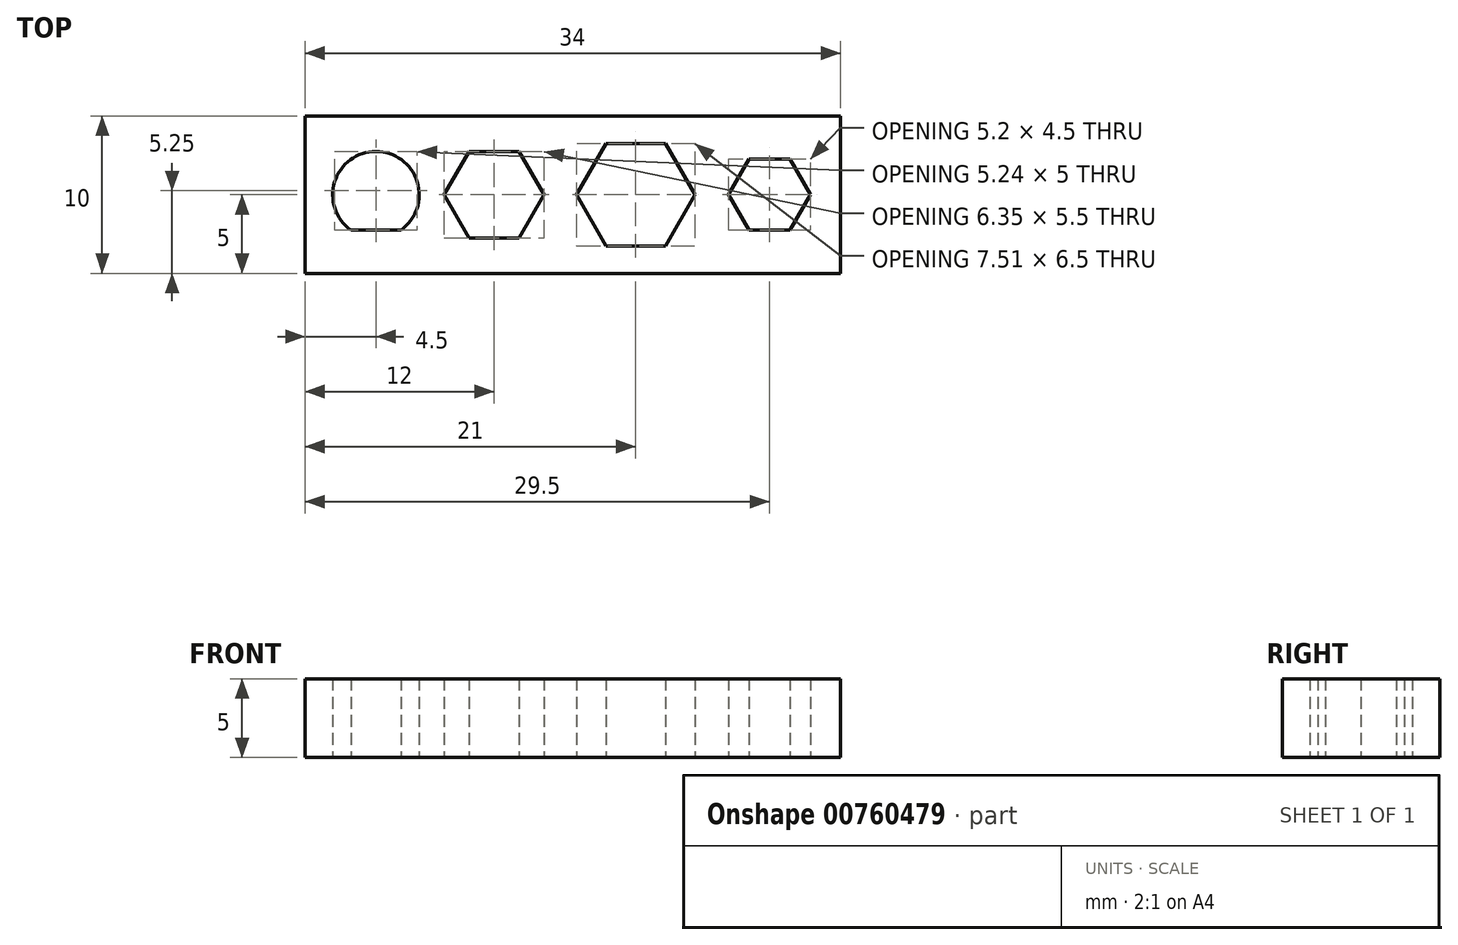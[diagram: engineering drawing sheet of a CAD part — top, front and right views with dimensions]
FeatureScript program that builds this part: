
annotation { "Feature Type Name" : "Feature", "Feature Type Description" : "" }
export const myFeature = defineFeature(function(context is Context, id is Id, definition is map)
    precondition{}
    {
        {
            var Q0;
            Q0=qCreatedBy(makeId("Top.planeOp"),FACE);
            var sketch = newSketch(context, id + "F0", { "sketchPlane" : qUnion([Q0])});
            skPoint(sketch, "E0.middle", {"position": v(0, 0) * mm});
            skCircle(sketch, "E1", {"center": v(-7.5, 0) * mm, "radius": 2.75 * mm});
            skCircle(sketch, "E2.cCircle", {"center": v(9, 0) * mm, "radius": 3.25 * mm, "construction": true});
            skLineSegment(sketch, "E2.0", {"start": v(7.12, 3.25) * mm, "end": v(10.88, 3.25) * mm});
            skLineSegment(sketch, "E2.1", {"start": v(10.88, 3.25) * mm, "end": v(12.75, 0) * mm});
            skLineSegment(sketch, "E2.2", {"start": v(12.75, 0) * mm, "end": v(10.88, -3.25) * mm});
            skLineSegment(sketch, "E2.3", {"start": v(10.88, -3.25) * mm, "end": v(7.12, -3.25) * mm});
            skLineSegment(sketch, "E2.4", {"start": v(7.12, -3.25) * mm, "end": v(5.25, 0) * mm});
            skLineSegment(sketch, "E2.5", {"start": v(5.25, 0) * mm, "end": v(7.12, 3.25) * mm});
            skPoint(sketch, "E2.0.midPoint", {"position": v(9, 3.25) * mm});
            skCircle(sketch, "E3.cCircle", {"center": v(0, 0) * mm, "radius": 2.75 * mm, "construction": true});
            skLineSegment(sketch, "E3.0", {"start": v(-1.59, 2.75) * mm, "end": v(1.59, 2.75) * mm});
            skLineSegment(sketch, "E3.1", {"start": v(1.59, 2.75) * mm, "end": v(3.18, 0) * mm});
            skLineSegment(sketch, "E3.2", {"start": v(3.18, 0) * mm, "end": v(1.59, -2.75) * mm});
            skLineSegment(sketch, "E3.3", {"start": v(1.59, -2.75) * mm, "end": v(-1.59, -2.75) * mm});
            skLineSegment(sketch, "E3.4", {"start": v(-1.59, -2.75) * mm, "end": v(-3.18, 0) * mm});
            skLineSegment(sketch, "E3.5", {"start": v(-3.18, 0) * mm, "end": v(-1.59, 2.75) * mm});
            skPoint(sketch, "E3.0.midPoint", {"position": v(0, 2.75) * mm});
            skLineSegment(sketch, "E4", {"start": v(-9.08, -2.25) * mm, "end": v(-5.92, -2.25) * mm});
            skLineSegment(sketch, "E5", {"start": v(-7.5, 0) * mm, "end": v(-7.5, -2.75) * mm, "construction": true});
            skLineSegment(sketch, "E6.bottom", {"start": v(-12, 5) * mm, "end": v(22, 5) * mm});
            skLineSegment(sketch, "E6.top", {"start": v(-12, -5) * mm, "end": v(22, -5) * mm});
            skLineSegment(sketch, "E6.left", {"start": v(-12, 5) * mm, "end": v(-12, -5) * mm});
            skLineSegment(sketch, "E6.right", {"start": v(22, 5) * mm, "end": v(22, -5) * mm});
            skCircle(sketch, "E7.cCircle", {"center": v(17.5, 0) * mm, "radius": 2.25 * mm, "construction": true});
            skLineSegment(sketch, "E7.0", {"start": v(18.8, -2.25) * mm, "end": v(16.2, -2.25) * mm});
            skLineSegment(sketch, "E7.1", {"start": v(16.2, -2.25) * mm, "end": v(14.9, 0) * mm});
            skLineSegment(sketch, "E7.2", {"start": v(14.9, 0) * mm, "end": v(16.2, 2.25) * mm});
            skLineSegment(sketch, "E7.3", {"start": v(16.2, 2.25) * mm, "end": v(18.8, 2.25) * mm});
            skLineSegment(sketch, "E7.4", {"start": v(18.8, 2.25) * mm, "end": v(20.1, 0) * mm});
            skLineSegment(sketch, "E7.5", {"start": v(20.1, 0) * mm, "end": v(18.8, -2.25) * mm});
            skPoint(sketch, "E7.0.midPoint", {"position": v(17.5, -2.25) * mm});
            skSolve(sketch);
        }
        {
            var Q0;
            Q0=makeQuery(id+"F0.imprint","IMPRINT",FACE,{"disambiguationData":[TD([[makeQuery(id+"F0.imprint","IMPRINT",EDGE,{"derivedFrom":sQuery(id+"F0.wireOp",EDGE,"E2.0")}),1.0]])]});
            var Q1;
            {var subQ0=sQuery(id+"F0.wireOp",EDGE,"E4");Q1=makeQuery(id+"F0.imprint","IMPRINT",FACE,{"disambiguationData":[TD([[makeQuery(id+"F0.imprint","IMPRINT",EDGE,{"derivedFrom":subQ0}),-1.0]])]});}
            extrude(context, id + "F1", {"entities" : qUnion([Q0, Q1]), "depth" : 5 * mm, "offsetDistance" : 25 * mm});
        }
    });
